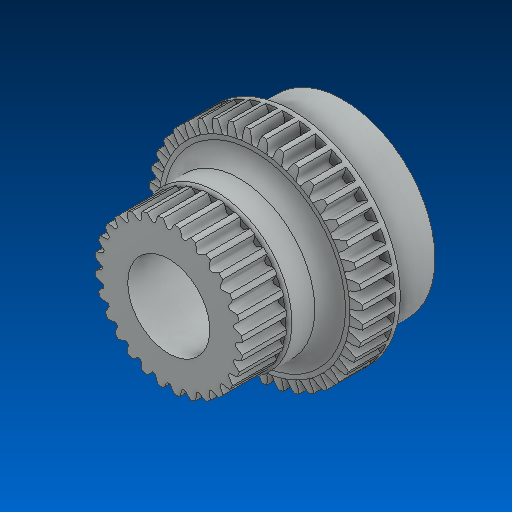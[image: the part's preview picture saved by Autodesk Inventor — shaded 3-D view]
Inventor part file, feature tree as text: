
AUTODESK INVENTOR PART (.ipt)
format: ipt  version: 2022.2 (Build 262287000, 287)  size: 1,149,952 bytes
history: native  units: in
note: dims shown in document units (in); Inventor stores cm internally (conversion verified against a paired STEP export)
features: fillet x1
ambient origin geometry x8: Origin, YZ Plane, XZ Plane, XY Plane, X Axis, Y Axis, Z Axis, Center Point
bodies: Solid1 (feature_tree)
feature tree (1):
  fillet  "Fillet5"  [1 undecoded]
note: 1 required parameter value undecoded (feature->parameter linkage not recoverable at this tier; creation-order binding heuristic only, values carry confidence <= 0.55)
